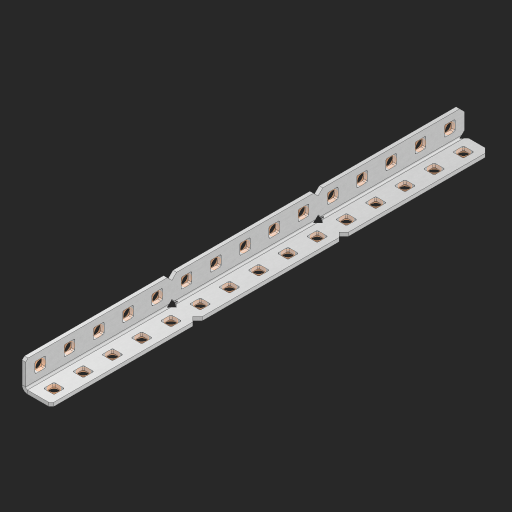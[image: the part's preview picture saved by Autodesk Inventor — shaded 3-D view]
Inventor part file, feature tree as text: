
AUTODESK INVENTOR PART (.ipt)
format: ipt  version: 2023 (Build 270158000, 158)  size: 709,120 bytes
history: native  units: in
note: dims shown in document units (in); Inventor stores cm internally (conversion verified against a paired STEP export)
features: other x36, extrude x31, sheet_metal_op x8, sketch x5, pattern_linear x1, mirror x1, chamfer x1
ambient origin geometry x8: Origin, YZ Plane, XZ Plane, XY Plane, X Axis, Y Axis, Z Axis, Center Point
bodies: Solid1 (feature_tree), Body (feature_tree)
feature tree (83):
  sheet_metal_op  "Flanges"
  sheet_metal_op  "Body Pattern"
  other  "Arc Length"
  pattern_linear  "Notch Pattern"  Spacing1=0.125in  [1 undecoded]
  other  "Diagonal Plane"
  mirror  "Everything Mirrored"
  chamfer  "End Chamfer"
  sketch  "Sketch1"  dims[d0=0.5in]
  other  "Plate1"
  sketch  "Sketch2"  dims[d1=7.5in]
  other  "Plate2"
  sheet_metal_op  "Bend1"
  sheet_metal_op  "Corner1"
  sketch  "Sketch8"  dims[d2=0.0625in]
  sketch  "Sketch9"  dims[d3=0.0625in]
  other  "Srf91"
  sheet_metal_op  "Body Pattern Sketch"
  other  "Srf92"
  sketch  "Sketch13"  dims[d4=0.0312in d5=0.125in d6=0.0625in d7=0.5in d8=90.0deg d9=0.0312in d10=0.25in d11=0.0625in d12=0.0625in d49=0.182in d50=0.02in d52=0.25in d53=0.0625in d54=0.0in d55=0.172in d56=1.0in d57=0.0in d85=0.1473in d86=0.1782in d89=0.0625in d90=0.0in d91=0.04in d92=0.0491in d95=2.5in d96=0.04in d97=0.25in d98=45.0deg d123=0.204in d126=0.0491in d127=0.1473in d128=0.08in d129=0.04in d130=2.5in d131=5.9055in d133=0.5in d134=0.3937in d136=1.0in]
  other  "Srf856"
  other  "Srf857"
  other  "Srf858"
  other  "Srf859"
  other  "Srf860"
  other  "Srf861"
  other  "Srf1275"
  other  "Srf1276"
  other  "Srf1278"
  other  "Srf1279"
  other  "Srf1280"
  other  "Srf1281"
  other  "Srf1282"
  other  "Srf1283"
  other  "Srf1383"
  other  "Srf1384"
  other  "Srf1385"
  other  "Srf1386"
  other  "Srf1387"
  other  "Srf1388"
  other  "Srf1389"
  other  "Srf1390"
  other  "Srf1475"
  other  "Srf1476"
  other  "Srf1477"
  other  "Srf1478"
  other  "Srf1479"
  other  "Srf1480"
  other  "Srf1481"
  other  "Srf1482"
  sheet_metal_op  "Body Stamp"
  sheet_metal_op  "Body Circle"
  sheet_metal_op  "Notch"
  extrude  "ExtrusionSrf92"  Depth=0.0625in
  extrude  "ExtrusionSrf856"  Depth=0.5in TaperAngle=90.0deg
  extrude  "ExtrusionSrf857"  Depth=0.25in
  extrude  "ExtrusionSrf858"  Depth=0.0625in
  extrude  "ExtrusionSrf859"  Depth=0.0625in
  extrude  "ExtrusionSrf860"  Depth=0.3937in
  extrude  "ExtrusionSrf861"  Depth=0.3937in
  extrude  "ExtrusionSrf1275"  Depth=0.25in
  extrude  "ExtrusionSrf1276"  Depth=0.0625in
  extrude  "ExtrusionSrf1277"  TaperAngle=0.0deg  [1 undecoded]
  extrude  "ExtrusionSrf1278"  Depth=0.3937in
  extrude  "ExtrusionSrf1279"  Depth=0.3937in TaperAngle=0.0deg
  extrude  "ExtrusionSrf1280"  Depth=0.3937in
  extrude  "ExtrusionSrf1281"  Depth=0.3937in
  extrude  "ExtrusionSrf1282"  Depth=0.0625in
  extrude  "ExtrusionSrf1383"  Depth=0.3937in TaperAngle=0.0deg
  extrude  "ExtrusionSrf1384"  Depth=0.3937in
  extrude  "ExtrusionSrf1385"  Depth=0.25in TaperAngle=45.0deg
  extrude  "ExtrusionSrf1386"  Depth=0.3937in
  extrude  "ExtrusionSrf1387"  Depth=0.3937in
  extrude  "ExtrusionSrf1388"  Depth=0.3937in
  extrude  "ExtrusionSrf1389"  Depth=0.3937in
  extrude  "ExtrusionSrf1390"  Depth=0.3937in
  extrude  "ExtrusionSrf1475"  Depth=0.3937in
  extrude  "ExtrusionSrf1476"  Depth=0.3937in
  extrude  "ExtrusionSrf1477"  Depth=0.5in
  extrude  "ExtrusionSrf1478"  [1 undecoded]
  extrude  "ExtrusionSrf1479"  [1 undecoded]
  extrude  "ExtrusionSrf1480"  [1 undecoded]
  extrude  "ExtrusionSrf1481"  [1 undecoded]
  extrude  "ExtrusionSrf1482"  [1 undecoded]
note: 7 required parameter values undecoded (feature->parameter linkage not recoverable at this tier; creation-order binding heuristic only, values carry confidence <= 0.55)
